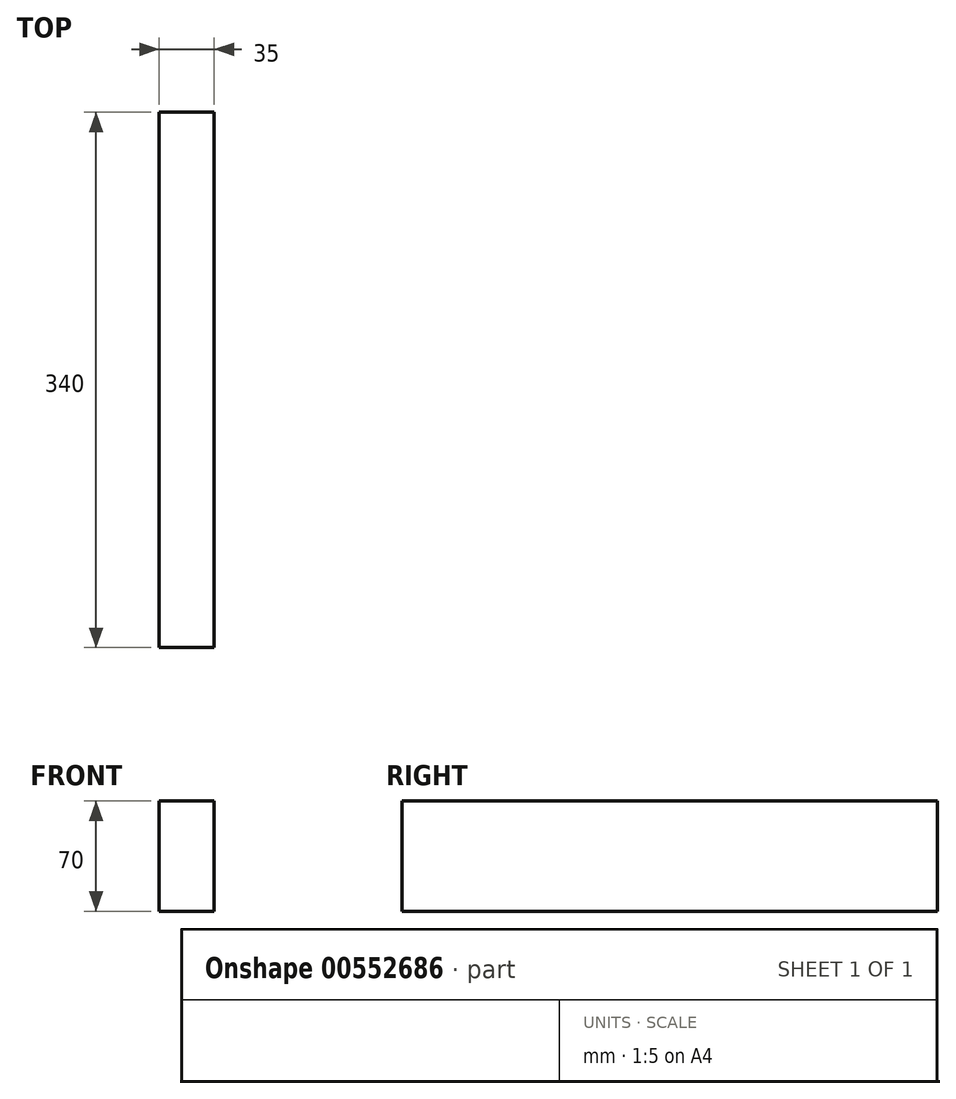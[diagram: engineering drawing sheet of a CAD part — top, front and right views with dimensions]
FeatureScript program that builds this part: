
annotation { "Feature Type Name" : "Feature", "Feature Type Description" : "" }
export const myFeature = defineFeature(function(context is Context, id is Id, definition is map)
    precondition{}
    {
        {
            var Q0;
            Q0=qCreatedBy(makeId("Front.planeOp"),FACE);
            var sketch = newSketch(context, id + "F0", { "sketchPlane" : qUnion([Q0])});
            skLineSegment(sketch, "E0.bottom", {"start": v(17.5, 35) * mm, "end": v(-17.5, 35) * mm});
            skLineSegment(sketch, "E0.top", {"start": v(17.5, -35) * mm, "end": v(-17.5, -35) * mm});
            skLineSegment(sketch, "E0.left", {"start": v(17.5, 35) * mm, "end": v(17.5, -35) * mm});
            skLineSegment(sketch, "E0.right", {"start": v(-17.5, 35) * mm, "end": v(-17.5, -35) * mm});
            skPoint(sketch, "E0.middle", {"position": v(0, 0) * mm});
            skSolve(sketch);
        }
        {
            var Q0;
            Q0 = qSketchRegion(id + "F0", true);
            extrude(context, id + "F1", {"entities" : qUnion([Q0]), "oppositeDirection" : true, "depth" : 340 * mm, "offsetDistance" : 25 * mm});
        }
    });
